# Revit family: P210876JX-001_JUIFN15HX
name_source: partatom
category: Specialty Equipment
units: mm (PartAtom-declared; Revit-internal decimal feet)

## family parameters
Always vertical = Yes
Cut with Voids When Loaded = No
Enable Cutting in Views = No
Maintain Annotation Orientation = No
Part Type = Normal
Room Calculation Point = No
Round Connector Dimension = Use Diameter
Shared = No
Work Plane-Based = No

## types (1)
- JUIFN15HX
    Amps = 0 A
    Back Panel Material = ARCAT - Metal - Aluminum
    Body Material = ARCAT - Metal - Steel - Black
    Bottom Panel Material = ARCAT - Metal - Steel - Black
    Clearance Material = ARCAT - Clearance
    Default Elevation = 0"
    Depth = 24"
    Description = Panel-Ready 15" Undercounter Ice Machine with Articulating Hinge
Machine à glaçons sous le comptoir avec charnière articulée, prête pour le panneau de recouvrement, 15 po
    Dimension Guide = https://whirlpool.com
https://whirlpool.com
    Door Material = ARCAT - Metal - Steel - Black - Light
    Family Name = Built-In Ice Maker
    Feature 1 = Stealth Flush Design
Stealth Flush Design
    Feature 2 = Crystalline Ice
Glace cristalline
    Feature 3 = Max Ice Option
Option de glaçons accélérés
    Handle Material = ARCAT - Metal - Brass
    Height = 33 3/4"
    Hinge Material = ARCAT - Plastic - Black
    Installation-Fabrication = https://whirlpool.com
https://whirlpool.com
    Leg Material = ARCAT - Plastic - Black
    Manufacturer = JennAir
    Model = JUIFN15HX
    Right Swing = Yes
    Screw Material = ARCAT - Metal - Steel - Stainless
    Voltage = 0 V
    Width = 15"

## geometry (parser evidence)
native form markers: Sweep x2
no freeform markers — native parametric forms only
